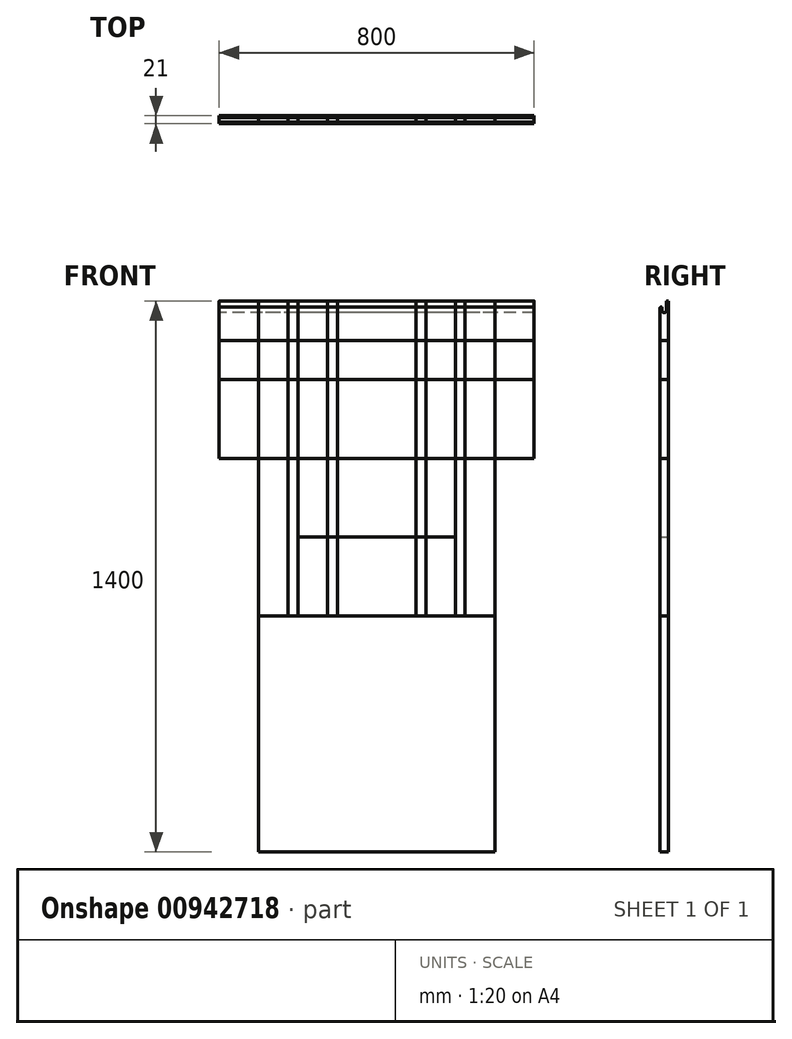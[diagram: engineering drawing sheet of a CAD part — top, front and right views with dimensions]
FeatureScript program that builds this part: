
annotation { "Feature Type Name" : "Feature", "Feature Type Description" : "" }
export const myFeature = defineFeature(function(context is Context, id is Id, definition is map)
    precondition{}
    {
        {
            var Q0;
            Q0=qCreatedBy(makeId("Right.planeOp"),FACE);
            var sketch = newSketch(context, id + "F0", { "sketchPlane" : qUnion([Q0])});
            skLineSegment(sketch, "E0", {"start": v(8, 407.5) * mm, "end": v(8, 407.5) * mm});
            skLineSegment(sketch, "E1", {"start": v(5.5, 405) * mm, "end": v(5.5, 383) * mm});
            skLineSegment(sketch, "E2", {"start": v(0, 377.5) * mm, "end": v(0, 377.5) * mm});
            skLineSegment(sketch, "E3", {"start": v(-5.5, 383) * mm, "end": v(-5.5, 390) * mm});
            skLineSegment(sketch, "E4", {"start": v(-8, 392.5) * mm, "end": v(-8, 392.5) * mm});
            skLineSegment(sketch, "E5", {"start": v(-10.5, 390) * mm, "end": v(-10.5, -392.5) * mm});
            skLineSegment(sketch, "E6", {"start": v(-10.5, -392.5) * mm, "end": v(10.5, -392.5) * mm});
            skLineSegment(sketch, "E7", {"start": v(10.5, 407.5) * mm, "end": v(10.5, -392.5) * mm});
            skLineSegment(sketch, "E8", {"start": v(-10.5, 0) * mm, "end": v(0, 0) * mm, "construction": true});
            skLineSegment(sketch, "E9", {"start": v(0, 0) * mm, "end": v(10.5, 0) * mm, "construction": true});
            skPoint(sketch, "E10.visualSharp", {"position": v(5.5, 407.5) * mm});
            skArc(sketch, "E10.filletArc", {"start": v(8, 407.5) * mm, "mid": v(6.23, 406.77) * mm, "end": v(5.5, 405) * mm});
            skPoint(sketch, "E11.visualSharp", {"position": v(-10.5, 392.5) * mm});
            skArc(sketch, "E11.filletArc", {"start": v(-8, 392.5) * mm, "mid": v(-9.77, 391.77) * mm, "end": v(-10.5, 390) * mm});
            skPoint(sketch, "E12.visualSharp", {"position": v(-5.5, 392.5) * mm});
            skArc(sketch, "E12.filletArc", {"start": v(-5.5, 390) * mm, "mid": v(-6.23, 391.77) * mm, "end": v(-8, 392.5) * mm});
            skPoint(sketch, "E13.visualSharp", {"position": v(-5.5, 377.5) * mm});
            skArc(sketch, "E13.filletArc", {"start": v(-5.5, 383) * mm, "mid": v(-3.89, 379.11) * mm, "end": v(0, 377.5) * mm});
            skPoint(sketch, "E14.visualSharp", {"position": v(5.5, 377.5) * mm});
            skArc(sketch, "E14.filletArc", {"start": v(0, 377.5) * mm, "mid": v(3.89, 379.11) * mm, "end": v(5.5, 383) * mm});
            skPoint(sketch, "E15.visualSharp", {"position": v(10.5, 407.5) * mm});
            skLineSegment(sketch, "E16", {"start": v(-10.5, 7.5) * mm, "end": v(10.5, 7.5) * mm});
            skLineSegment(sketch, "E17", {"start": v(10.5, 207.5) * mm, "end": v(-10.5, 207.5) * mm});
            skLineSegment(sketch, "E18", {"start": v(-10.5, 307.5) * mm, "end": v(10.5, 307.5) * mm});
            skLineSegment(sketch, "E19", {"start": v(8, 407.5) * mm, "end": v(10.5, 407.5) * mm});
            skLineSegment(sketch, "E20", {"start": v(-10.5, -192.5) * mm, "end": v(10.5, -192.5) * mm});
            skLineSegment(sketch, "E21.top", {"start": v(-10.5, -992.5) * mm, "end": v(10.5, -992.5) * mm});
            skLineSegment(sketch, "E21.left", {"start": v(-10.5, -392.5) * mm, "end": v(-10.5, -992.5) * mm});
            skLineSegment(sketch, "E21.right", {"start": v(10.5, -392.5) * mm, "end": v(10.5, -992.5) * mm});
            skSolve(sketch);
        }
        {
            var Q0;
            Q0=makeQuery(id+"F0.imprint","IMPRINT",FACE,{"disambiguationData":[TD([[makeQuery(id+"F0.imprint","IMPRINT",EDGE,{"derivedFrom":sQuery(id+"F0.wireOp",EDGE,"E1")}),1.0]])]});
            var Q1;
            {var subQ0=sQuery(id+"F0.wireOp",EDGE,"E17");Q1=makeQuery(id+"F0.imprint","IMPRINT",FACE,{"disambiguationData":[TD([[makeQuery(id+"F0.imprint","IMPRINT",EDGE,{"derivedFrom":subQ0}),-1.0]])]});}
            var Q2;
            {var subQ0=sQuery(id+"F0.wireOp",EDGE,"E16");Q2=makeQuery(id+"F0.imprint","IMPRINT",FACE,{"disambiguationData":[TD([[makeQuery(id+"F0.imprint","IMPRINT",EDGE,{"derivedFrom":subQ0}),1.0]])]});}
            var Q3;
            {var subQ0=sQuery(id+"F0.wireOp",EDGE,"E16");Q3=makeQuery(id+"F0.imprint","IMPRINT",FACE,{"disambiguationData":[TD([[makeQuery(id+"F0.imprint","IMPRINT",EDGE,{"derivedFrom":subQ0}),-1.0]])]});}
            var Q4;
            {var subQ2=sQuery(id+"F0.wireOp",EDGE,"E20");Q4=makeQuery(id+"F0.imprint","IMPRINT",FACE,{"disambiguationData":[TD([[makeQuery(id+"F0.imprint","IMPRINT",EDGE,{"derivedFrom":subQ2}),-1.0]])]});}
            extrude(context, id + "F1", {"entities" : qUnion([Q0, Q1, Q2, Q3, Q4]), "depth" : 200 * mm, "offsetDistance" : 25 * mm, "symmetric" : true});
        }
        {
            var Q0;
            {var subQ2=sQuery(id+"F0.wireOp",EDGE,"E20");Q0=makeQuery(id+"F0.imprint","IMPRINT",FACE,{"disambiguationData":[TD([[makeQuery(id+"F0.imprint","IMPRINT",EDGE,{"derivedFrom":subQ2}),-1.0]])]});}
            var Q1;
            {var subQ0=sQuery(id+"F0.wireOp",EDGE,"E16");Q1=makeQuery(id+"F0.imprint","IMPRINT",FACE,{"disambiguationData":[TD([[makeQuery(id+"F0.imprint","IMPRINT",EDGE,{"derivedFrom":subQ0}),-1.0]])]});}
            var Q2;
            {var subQ0=sQuery(id+"F0.wireOp",EDGE,"E16");Q2=makeQuery(id+"F0.imprint","IMPRINT",FACE,{"disambiguationData":[TD([[makeQuery(id+"F0.imprint","IMPRINT",EDGE,{"derivedFrom":subQ0}),1.0]])]});}
            var Q3;
            {var subQ0=sQuery(id+"F0.wireOp",EDGE,"E17");Q3=makeQuery(id+"F0.imprint","IMPRINT",FACE,{"disambiguationData":[TD([[makeQuery(id+"F0.imprint","IMPRINT",EDGE,{"derivedFrom":subQ0}),-1.0]])]});}
            var Q4;
            Q4=makeQuery(id+"F0.imprint","IMPRINT",FACE,{"disambiguationData":[TD([[makeQuery(id+"F0.imprint","IMPRINT",EDGE,{"derivedFrom":sQuery(id+"F0.wireOp",EDGE,"E1")}),1.0]])]});
            extrude(context, id + "F2", {"entities" : qUnion([Q0, Q1, Q2, Q3, Q4]), "depth" : 250 * mm, "offsetDistance" : 25 * mm, "symmetric" : true});
        }
        {
            var Q0;
            {var subQ2=sQuery(id+"F0.wireOp",EDGE,"E20");Q0=makeQuery(id+"F0.imprint","IMPRINT",FACE,{"disambiguationData":[TD([[makeQuery(id+"F0.imprint","IMPRINT",EDGE,{"derivedFrom":subQ2}),-1.0]])]});}
            var Q1;
            {var subQ0=sQuery(id+"F0.wireOp",EDGE,"E16");Q1=makeQuery(id+"F0.imprint","IMPRINT",FACE,{"disambiguationData":[TD([[makeQuery(id+"F0.imprint","IMPRINT",EDGE,{"derivedFrom":subQ0}),-1.0]])]});}
            var Q2;
            {var subQ0=sQuery(id+"F0.wireOp",EDGE,"E16");Q2=makeQuery(id+"F0.imprint","IMPRINT",FACE,{"disambiguationData":[TD([[makeQuery(id+"F0.imprint","IMPRINT",EDGE,{"derivedFrom":subQ0}),1.0]])]});}
            var Q3;
            {var subQ0=sQuery(id+"F0.wireOp",EDGE,"E17");Q3=makeQuery(id+"F0.imprint","IMPRINT",FACE,{"disambiguationData":[TD([[makeQuery(id+"F0.imprint","IMPRINT",EDGE,{"derivedFrom":subQ0}),-1.0]])]});}
            var Q4;
            Q4=makeQuery(id+"F0.imprint","IMPRINT",FACE,{"disambiguationData":[TD([[makeQuery(id+"F0.imprint","IMPRINT",EDGE,{"derivedFrom":sQuery(id+"F0.wireOp",EDGE,"E1")}),1.0]])]});
            extrude(context, id + "F3", {"entities" : qUnion([Q0, Q1, Q2, Q3, Q4]), "depth" : 400 * mm, "offsetDistance" : 25 * mm, "symmetric" : true});
        }
        {
            var Q0;
            Q0=makeQuery(id+"F0.imprint","IMPRINT",FACE,{"disambiguationData":[TD([[makeQuery(id+"F0.imprint","IMPRINT",EDGE,{"derivedFrom":sQuery(id+"F0.wireOp",EDGE,"E1")}),1.0]])]});
            var Q1;
            {var subQ0=sQuery(id+"F0.wireOp",EDGE,"E17");Q1=makeQuery(id+"F0.imprint","IMPRINT",FACE,{"disambiguationData":[TD([[makeQuery(id+"F0.imprint","IMPRINT",EDGE,{"derivedFrom":subQ0}),-1.0]])]});}
            var Q2;
            {var subQ0=sQuery(id+"F0.wireOp",EDGE,"E16");Q2=makeQuery(id+"F0.imprint","IMPRINT",FACE,{"disambiguationData":[TD([[makeQuery(id+"F0.imprint","IMPRINT",EDGE,{"derivedFrom":subQ0}),1.0]])]});}
            var Q3;
            {var subQ0=sQuery(id+"F0.wireOp",EDGE,"E16");Q3=makeQuery(id+"F0.imprint","IMPRINT",FACE,{"disambiguationData":[TD([[makeQuery(id+"F0.imprint","IMPRINT",EDGE,{"derivedFrom":subQ0}),-1.0]])]});}
            var Q4;
            {var subQ2=sQuery(id+"F0.wireOp",EDGE,"E20");Q4=makeQuery(id+"F0.imprint","IMPRINT",FACE,{"disambiguationData":[TD([[makeQuery(id+"F0.imprint","IMPRINT",EDGE,{"derivedFrom":subQ2}),-1.0]])]});}
            extrude(context, id + "F4", {"entities" : qUnion([Q0, Q1, Q2, Q3, Q4]), "depth" : 600 * mm, "offsetDistance" : 25 * mm, "symmetric" : true});
        }
        {
            var Q0;
            Q0=makeQuery(id+"F0.imprint","IMPRINT",FACE,{"disambiguationData":[TD([[makeQuery(id+"F0.imprint","IMPRINT",EDGE,{"derivedFrom":sQuery(id+"F0.wireOp",EDGE,"E1")}),1.0]])]});
            var Q1;
            {var subQ0=sQuery(id+"F0.wireOp",EDGE,"E17");Q1=makeQuery(id+"F0.imprint","IMPRINT",FACE,{"disambiguationData":[TD([[makeQuery(id+"F0.imprint","IMPRINT",EDGE,{"derivedFrom":subQ0}),-1.0]])]});}
            extrude(context, id + "F5", {"entities" : qUnion([Q0, Q1]), "depth" : 400 * mm, "offsetDistance" : 25 * mm, "symmetric" : true});
        }
        {
            var Q0;
            Q0=makeQuery(id+"F0.imprint","IMPRINT",FACE,{"disambiguationData":[TD([[makeQuery(id+"F0.imprint","IMPRINT",EDGE,{"derivedFrom":sQuery(id+"F0.wireOp",EDGE,"E1")}),1.0]])]});
            extrude(context, id + "F6", {"entities" : qUnion([Q0]), "depth" : 800 * mm, "offsetDistance" : 25 * mm, "symmetric" : true});
        }
        {
            var Q0;
            Q0=makeQuery(id+"F0.imprint","IMPRINT",FACE,{"disambiguationData":[TD([[makeQuery(id+"F0.imprint","IMPRINT",EDGE,{"derivedFrom":sQuery(id+"F0.wireOp",EDGE,"E1")}),1.0]])]});
            var Q1;
            {var subQ0=sQuery(id+"F0.wireOp",EDGE,"E17");Q1=makeQuery(id+"F0.imprint","IMPRINT",FACE,{"disambiguationData":[TD([[makeQuery(id+"F0.imprint","IMPRINT",EDGE,{"derivedFrom":subQ0}),-1.0]])]});}
            extrude(context, id + "F7", {"entities" : qUnion([Q0, Q1]), "depth" : 800 * mm, "offsetDistance" : 25 * mm, "symmetric" : true});
        }
        {
            var Q0;
            {var subQ0=sQuery(id+"F0.wireOp",EDGE,"E16");Q0=makeQuery(id+"F0.imprint","IMPRINT",FACE,{"disambiguationData":[TD([[makeQuery(id+"F0.imprint","IMPRINT",EDGE,{"derivedFrom":subQ0}),1.0]])]});}
            var Q1;
            {var subQ0=sQuery(id+"F0.wireOp",EDGE,"E17");Q1=makeQuery(id+"F0.imprint","IMPRINT",FACE,{"disambiguationData":[TD([[makeQuery(id+"F0.imprint","IMPRINT",EDGE,{"derivedFrom":subQ0}),-1.0]])]});}
            var Q2;
            Q2=makeQuery(id+"F0.imprint","IMPRINT",FACE,{"disambiguationData":[TD([[makeQuery(id+"F0.imprint","IMPRINT",EDGE,{"derivedFrom":sQuery(id+"F0.wireOp",EDGE,"E1")}),1.0]])]});
            extrude(context, id + "F8", {"entities" : qUnion([Q0, Q1, Q2]), "depth" : 800 * mm, "offsetDistance" : 25 * mm, "symmetric" : true});
        }
        {
            var Q0;
            Q0=makeQuery(id+"F0.imprint","IMPRINT",FACE,{"disambiguationData":[TD([[makeQuery(id+"F0.imprint","IMPRINT",EDGE,{"derivedFrom":sQuery(id+"F0.wireOp",EDGE,"E1")}),1.0]])]});
            var Q1;
            {var subQ0=sQuery(id+"F0.wireOp",EDGE,"E17");Q1=makeQuery(id+"F0.imprint","IMPRINT",FACE,{"disambiguationData":[TD([[makeQuery(id+"F0.imprint","IMPRINT",EDGE,{"derivedFrom":subQ0}),-1.0]])]});}
            var Q2;
            {var subQ0=sQuery(id+"F0.wireOp",EDGE,"E16");Q2=makeQuery(id+"F0.imprint","IMPRINT",FACE,{"disambiguationData":[TD([[makeQuery(id+"F0.imprint","IMPRINT",EDGE,{"derivedFrom":subQ0}),1.0]])]});}
            extrude(context, id + "F9", {"entities" : qUnion([Q0, Q1, Q2]), "depth" : 400 * mm, "offsetDistance" : 25 * mm, "symmetric" : true});
        }
        {
            var Q0;
            Q0=makeQuery(id+"F0.imprint","IMPRINT",FACE,{"disambiguationData":[TD([[makeQuery(id+"F0.imprint","IMPRINT",EDGE,{"derivedFrom":sQuery(id+"F0.wireOp",EDGE,"E1")}),1.0]])]});
            var Q1;
            {var subQ0=sQuery(id+"F0.wireOp",EDGE,"E17");Q1=makeQuery(id+"F0.imprint","IMPRINT",FACE,{"disambiguationData":[TD([[makeQuery(id+"F0.imprint","IMPRINT",EDGE,{"derivedFrom":subQ0}),-1.0]])]});}
            var Q2;
            {var subQ0=sQuery(id+"F0.wireOp",EDGE,"E16");Q2=makeQuery(id+"F0.imprint","IMPRINT",FACE,{"disambiguationData":[TD([[makeQuery(id+"F0.imprint","IMPRINT",EDGE,{"derivedFrom":subQ0}),1.0]])]});}
            extrude(context, id + "F10", {"entities" : qUnion([Q0, Q1, Q2]), "depth" : 600 * mm, "offsetDistance" : 25 * mm, "symmetric" : true});
        }
        {
            var Q0;
            Q0=makeQuery(id+"F0.imprint","IMPRINT",FACE,{"disambiguationData":[TD([[makeQuery(id+"F0.imprint","IMPRINT",EDGE,{"derivedFrom":sQuery(id+"F0.wireOp",EDGE,"E1")}),1.0]])]});
            var Q1;
            {var subQ0=sQuery(id+"F0.wireOp",EDGE,"E17");Q1=makeQuery(id+"F0.imprint","IMPRINT",FACE,{"disambiguationData":[TD([[makeQuery(id+"F0.imprint","IMPRINT",EDGE,{"derivedFrom":subQ0}),-1.0]])]});}
            var Q2;
            {var subQ0=sQuery(id+"F0.wireOp",EDGE,"E16");Q2=makeQuery(id+"F0.imprint","IMPRINT",FACE,{"disambiguationData":[TD([[makeQuery(id+"F0.imprint","IMPRINT",EDGE,{"derivedFrom":subQ0}),1.0]])]});}
            var Q3;
            {var subQ0=sQuery(id+"F0.wireOp",EDGE,"E16");Q3=makeQuery(id+"F0.imprint","IMPRINT",FACE,{"disambiguationData":[TD([[makeQuery(id+"F0.imprint","IMPRINT",EDGE,{"derivedFrom":subQ0}),-1.0]])]});}
            extrude(context, id + "F11", {"entities" : qUnion([Q0, Q1, Q2, Q3]), "depth" : 400 * mm, "offsetDistance" : 25 * mm, "symmetric" : true});
        }
        {
            var Q0;
            Q0=makeQuery(id+"F0.imprint","IMPRINT",FACE,{"disambiguationData":[TD([[makeQuery(id+"F0.imprint","IMPRINT",EDGE,{"derivedFrom":sQuery(id+"F0.wireOp",EDGE,"E6")}),-1.0]])]});
            var Q1;
            {var subQ2=sQuery(id+"F0.wireOp",EDGE,"E20");Q1=makeQuery(id+"F0.imprint","IMPRINT",FACE,{"disambiguationData":[TD([[makeQuery(id+"F0.imprint","IMPRINT",EDGE,{"derivedFrom":subQ2}),-1.0]])]});}
            var Q2;
            {var subQ0=sQuery(id+"F0.wireOp",EDGE,"E16");Q2=makeQuery(id+"F0.imprint","IMPRINT",FACE,{"disambiguationData":[TD([[makeQuery(id+"F0.imprint","IMPRINT",EDGE,{"derivedFrom":subQ0}),-1.0]])]});}
            var Q3;
            {var subQ0=sQuery(id+"F0.wireOp",EDGE,"E16");Q3=makeQuery(id+"F0.imprint","IMPRINT",FACE,{"disambiguationData":[TD([[makeQuery(id+"F0.imprint","IMPRINT",EDGE,{"derivedFrom":subQ0}),1.0]])]});}
            var Q4;
            {var subQ0=sQuery(id+"F0.wireOp",EDGE,"E17");Q4=makeQuery(id+"F0.imprint","IMPRINT",FACE,{"disambiguationData":[TD([[makeQuery(id+"F0.imprint","IMPRINT",EDGE,{"derivedFrom":subQ0}),-1.0]])]});}
            var Q5;
            Q5=makeQuery(id+"F0.imprint","IMPRINT",FACE,{"disambiguationData":[TD([[makeQuery(id+"F0.imprint","IMPRINT",EDGE,{"derivedFrom":sQuery(id+"F0.wireOp",EDGE,"E1")}),1.0]])]});
            extrude(context, id + "F12", {"entities" : qUnion([Q0, Q1, Q2, Q3, Q4, Q5]), "depth" : 600 * mm, "offsetDistance" : 25 * mm, "symmetric" : true});
        }
        {
            var Q0;
            Q0=makeQuery(id+"F0.imprint","IMPRINT",FACE,{"disambiguationData":[TD([[makeQuery(id+"F0.imprint","IMPRINT",EDGE,{"derivedFrom":sQuery(id+"F0.wireOp",EDGE,"E1")}),1.0]])]});
            var Q1;
            {var subQ0=sQuery(id+"F0.wireOp",EDGE,"E17");Q1=makeQuery(id+"F0.imprint","IMPRINT",FACE,{"disambiguationData":[TD([[makeQuery(id+"F0.imprint","IMPRINT",EDGE,{"derivedFrom":subQ0}),-1.0]])]});}
            var Q2;
            {var subQ0=sQuery(id+"F0.wireOp",EDGE,"E16");Q2=makeQuery(id+"F0.imprint","IMPRINT",FACE,{"disambiguationData":[TD([[makeQuery(id+"F0.imprint","IMPRINT",EDGE,{"derivedFrom":subQ0}),1.0]])]});}
            var Q3;
            {var subQ0=sQuery(id+"F0.wireOp",EDGE,"E16");Q3=makeQuery(id+"F0.imprint","IMPRINT",FACE,{"disambiguationData":[TD([[makeQuery(id+"F0.imprint","IMPRINT",EDGE,{"derivedFrom":subQ0}),-1.0]])]});}
            var Q4;
            {var subQ2=sQuery(id+"F0.wireOp",EDGE,"E20");Q4=makeQuery(id+"F0.imprint","IMPRINT",FACE,{"disambiguationData":[TD([[makeQuery(id+"F0.imprint","IMPRINT",EDGE,{"derivedFrom":subQ2}),-1.0]])]});}
            extrude(context, id + "F13", {"entities" : qUnion([Q0, Q1, Q2, Q3, Q4]), "depth" : 450 * mm, "offsetDistance" : 25 * mm, "symmetric" : true});
        }
    });
